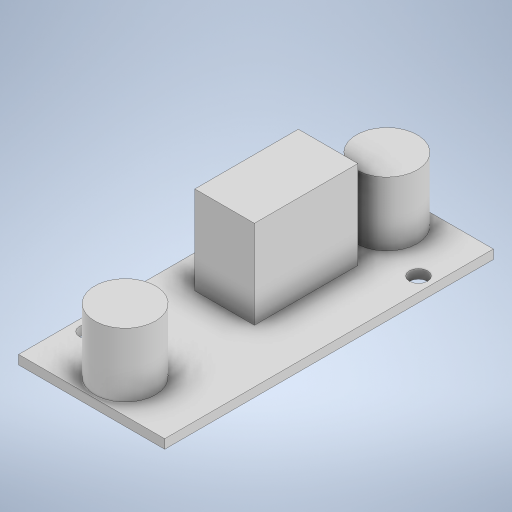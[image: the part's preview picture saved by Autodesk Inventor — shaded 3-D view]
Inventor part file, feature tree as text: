
AUTODESK INVENTOR PART (.ipt)
format: ipt  version: 2023 (Build 270158000, 158)  size: 265,216 bytes
history: native  units: mm
features: extrude x3, sketch x3, other x1
ambient origin geometry x8: Origin, YZ Plane, XZ Plane, XY Plane, X Axis, Y Axis, Z Axis, Center Point
bodies: Body1 (feature_tree)
feature tree (7):
  other  "솔리드1"
  extrude  "돌출1"  Depth=24.0mm
  extrude  "돌출2"  Depth=54.0mm
  extrude  "돌출3"  Depth=3.0mm
  sketch  "스케치1"
  sketch  "스케치2"
  sketch  "스케치3"
